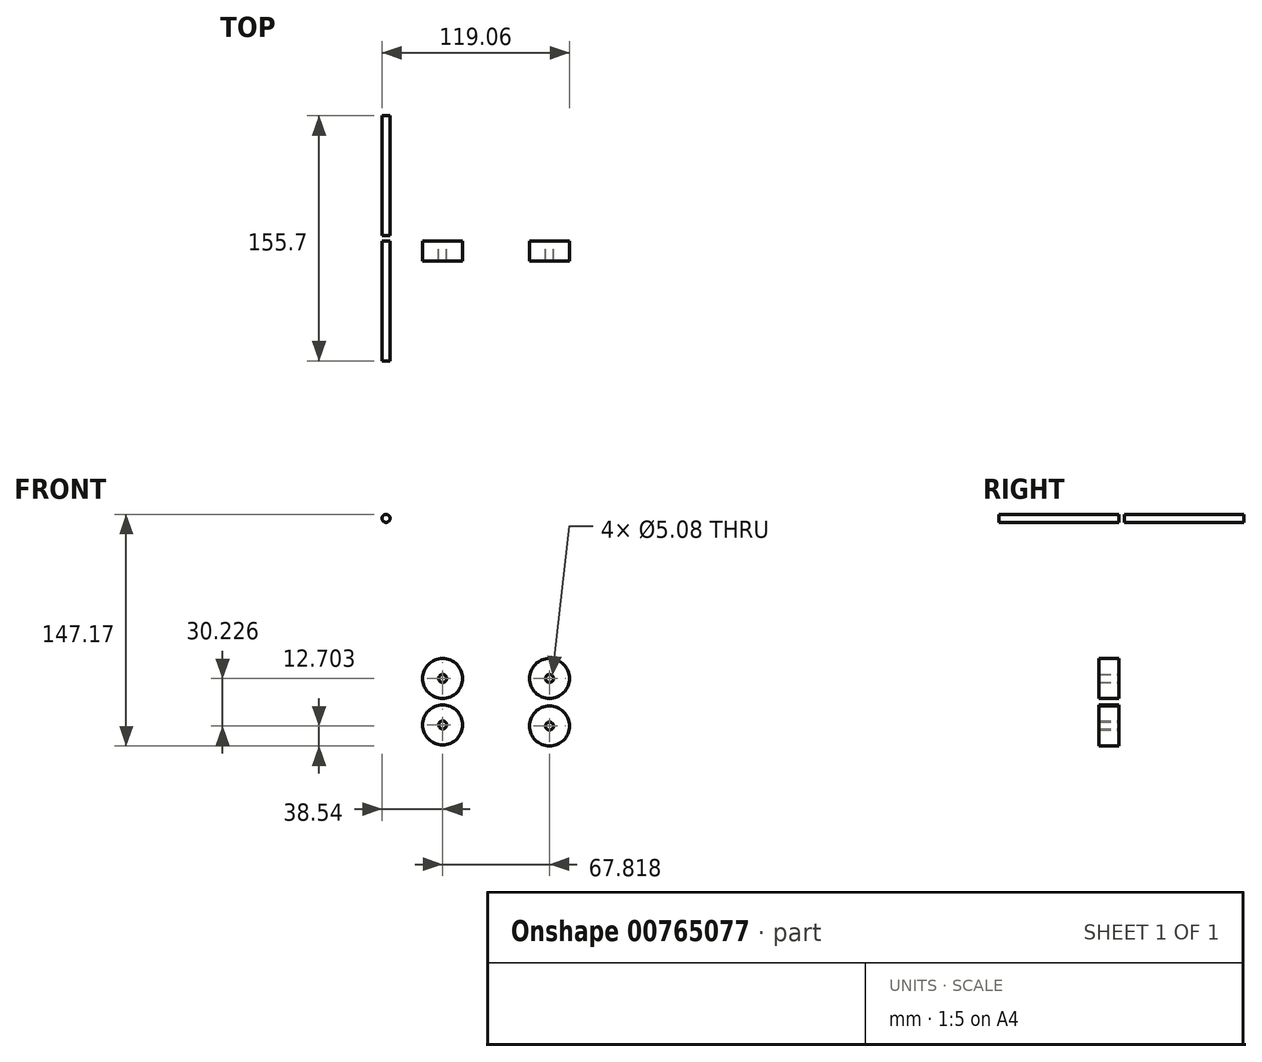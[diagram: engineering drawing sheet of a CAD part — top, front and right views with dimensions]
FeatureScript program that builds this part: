
annotation { "Feature Type Name" : "Feature", "Feature Type Description" : "" }
export const myFeature = defineFeature(function(context is Context, id is Id, definition is map)
    precondition{}
    {
        {
            var Q0;
            Q0=qCreatedBy(makeId("Front.planeOp"),FACE);
            var sketch = newSketch(context, id + "F0", { "sketchPlane" : qUnion([Q0])});
            skCircle(sketch, "E0", {"center": v(-35.07, -31.55) * mm, "radius": 12.7 * mm});
            skCircle(sketch, "E1", {"center": v(-35.07, -31.55) * mm, "radius": 2.54 * mm});
            skSolve(sketch);
        }
        {
            var Q0;
            Q0=makeQuery(id+"F0.imprint","IMPRINT",FACE,{"disambiguationData":[TD([[makeQuery(id+"F0.imprint","IMPRINT",EDGE,{"derivedFrom":sQuery(id+"F0.wireOp",EDGE,"E0")}),1.0]])]});
            var Q1;
            Q1=makeQuery(id+"F0.imprint","IMPRINT",FACE,{"disambiguationData":[TD([[makeQuery(id+"F0.imprint","IMPRINT",EDGE,{"derivedFrom":sQuery(id+"F0.wireOp",EDGE,"aaHtA2GT-CSYv-61oH-hfcB-drW0XoFWOrFK")}),1.0]])]});
            var Q2;
            Q2=makeQuery(id+"F0.imprint","IMPRINT",FACE,{"disambiguationData":[TD([[makeQuery(id+"F0.imprint","IMPRINT",EDGE,{"derivedFrom":sQuery(id+"F0.wireOp",EDGE,"b625252a-5020-4b6c-b3d7-88bc210e4772")}),1.0]])]});
            var Q3;
            Q3=makeQuery(id+"F0.imprint","IMPRINT",FACE,{"disambiguationData":[TD([[makeQuery(id+"F0.imprint","IMPRINT",EDGE,{"derivedFrom":sQuery(id+"F0.wireOp",EDGE,"6d6cb742-f04c-4b5e-88f4-180dd941e70a")}),1.0]])]});
            extrude(context, id + "F1", {"entities" : qUnion([Q0, Q1, Q2, Q3]), "depth" : 12.7 * mm, "offsetDistance" : 25.4 * mm});
        }
        {
            var Q0;
            Q0 = qSketchRegion(id + "F0", true);
            extrude(context, id + "F2", {"entities" : qUnion([Q0]), "operationType" : NewBodyOperationType.ADD, "depth" : 12.7 * mm, "offsetDistance" : 25.4 * mm});
        }
        {
            var Q0;
            Q0=makeQuery(id+"F1.opExtrude","SWEPT_BODY",BODY,{"disambiguationData":[OSD([sQuery(id+"F0.wireOp",EDGE,"E0"),sQuery(id+"F0.wireOp",EDGE,"E1")])]});
            transform(context, id + "F3", {"entities" : qUnion([Q0]), "transformType" : TransformType.TRANSLATION_3D, "dx" : 67.82 * mm, "dy" : 0 * mm, "dz" : 0 * mm, "makeCopy" : true});
        }
        {
            var Q0;
            Q0=makeQuery(id+"F3.opPattern","COPY",BODY,{"derivedFrom":makeQuery(id+"F1.opExtrude","SWEPT_BODY",BODY,{"disambiguationData":[OSD([sQuery(id+"F0.wireOp",EDGE,"E0"),sQuery(id+"F0.wireOp",EDGE,"E1")])]}),"instanceName":"1"});
            transform(context, id + "F4", {"entities" : qUnion([Q0]), "transformType" : TransformType.TRANSLATION_3D, "dx" : 0 * mm, "dy" : 0 * mm, "dz" : -30.23 * mm, "makeCopy" : true});
        }
        {
            var Q0;
            Q0=makeQuery(id+"F1.opExtrude","SWEPT_BODY",BODY,{"disambiguationData":[OSD([sQuery(id+"F0.wireOp",EDGE,"E0"),sQuery(id+"F0.wireOp",EDGE,"E1")])]});
            transform(context, id + "F5", {"entities" : qUnion([Q0]), "transformType" : TransformType.TRANSLATION_3D, "dx" : 0 * mm, "dy" : 0 * mm, "dz" : -29.46 * mm, "makeCopy" : true});
        }
        {
            var Q0;
            Q0=qCreatedBy(makeId("Front.planeOp"),FACE);
            var sketch = newSketch(context, id + "F6", { "sketchPlane" : qUnion([Q0])});
            skCircle(sketch, "E2", {"center": v(-71.07, 70.15) * mm, "radius": 2.54 * mm});
            skSolve(sketch);
        }
        {
            var Q0;
            Q0 = qSketchRegion(id + "F6", true);
            extrude(context, id + "F7", {"entities" : qUnion([Q0]), "depth" : 76.2 * mm, "offsetDistance" : 25.4 * mm});
        }
        {
            var Q0;
            Q0=makeQuery(id+"F7.opExtrude","SWEPT_BODY",BODY,{"disambiguationData":[OSD([sQuery(id+"F6.wireOp",EDGE,"E2")])]});
            transform(context, id + "F8", {"entities" : qUnion([Q0]), "transformType" : TransformType.TRANSLATION_3D, "dx" : 0 * mm, "dy" : 79.5 * mm, "dz" : 0 * mm, "makeCopy" : true});
        }
    });
